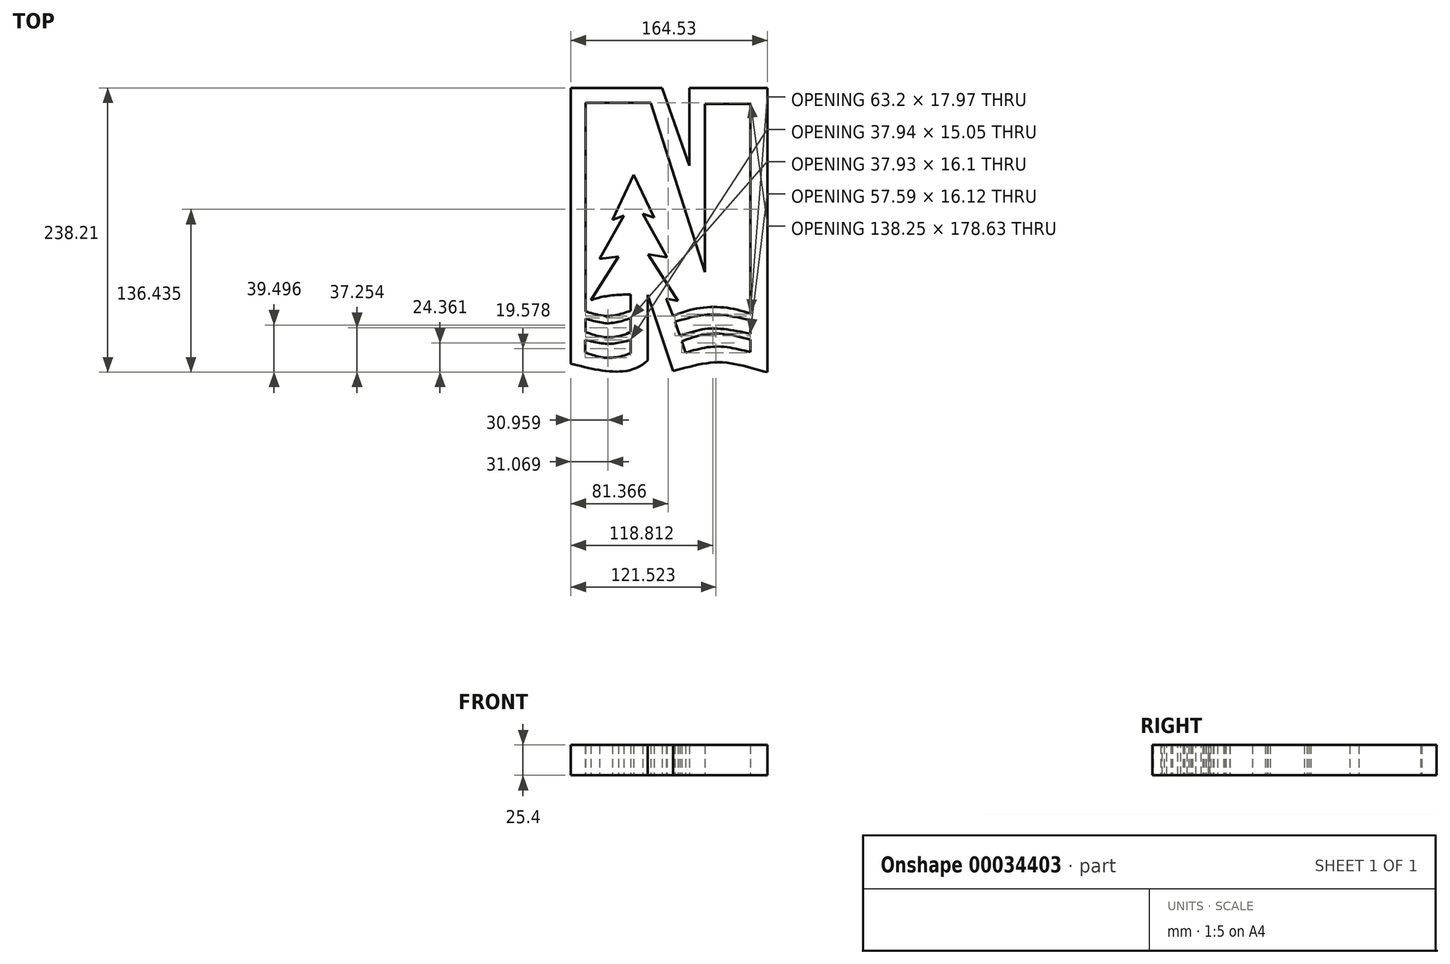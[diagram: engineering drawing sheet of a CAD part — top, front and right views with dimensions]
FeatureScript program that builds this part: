
annotation { "Feature Type Name" : "Feature", "Feature Type Description" : "" }
export const myFeature = defineFeature(function(context is Context, id is Id, definition is map)
    precondition{}
    {
        {
            var Q0;
            Q0=qCreatedBy(makeId("Top.planeOp"), FACE);
            var sketch = newSketch(context, id + "F0", { "sketchPlane" : qUnion([Q0])});
            skLineSegment(sketch, "E0", {"start": v(-73.6, 45.65) * mm, "end": v(-73.6, -185.45) * mm});
            skLineSegment(sketch, "E1", {"start": v(-73.6, 45.65) * mm, "end": v(2.84, 45.65) * mm});
            skLineSegment(sketch, "E2", {"start": v(2.84, 45.65) * mm, "end": v(25.57, -19.42) * mm});
            skLineSegment(sketch, "E3", {"start": v(25.57, -19.42) * mm, "end": v(25.57, 45.65) * mm});
            skLineSegment(sketch, "E4", {"start": v(25.57, 45.65) * mm, "end": v(90.93, 45.65) * mm});
            skLineSegment(sketch, "E5", {"start": v(90.93, 45.65) * mm, "end": v(90.93, -192.56) * mm});
            skLineSegment(sketch, "E6", {"start": v(12, -191.7) * mm, "end": v(-9.35, -127.62) * mm});
            skLineSegment(sketch, "E7", {"start": v(-9.35, -127.62) * mm, "end": v(-9.35, -182.72) * mm});
            skFitSpline(sketch, "E8", {"points": [v(90.93, -192.56) * mm, v(52.08, -184.29) * mm, v(12, -191.7) * mm], "startDerivative": vector(-76.55, 17.54) * mm, "endDerivative": vector(-80.4, -21.7) * mm});
            skFitSpline(sketch, "E9", {"points": [v(-9.35, -182.72) * mm, v(-39, -192) * mm, v(-73.6, -185.45) * mm], "startDerivative": vector(-50.09, -49.34) * mm, "endDerivative": vector(-64.77, 16.2) * mm});
            skLineSegment(sketch, "E10", {"start": v(-61.36, -141.64) * mm, "end": v(-61.36, 33.19) * mm});
            skLineSegment(sketch, "E11", {"start": v(-61.36, 33.19) * mm, "end": v(-6.84, 33.19) * mm});
            skLineSegment(sketch, "E12", {"start": v(-6.84, 33.19) * mm, "end": v(38.69, -108.6) * mm});
            skLineSegment(sketch, "E13", {"start": v(38.69, -108.6) * mm, "end": v(38.69, 32.2) * mm});
            skLineSegment(sketch, "E14", {"start": v(38.69, 32.2) * mm, "end": v(76.89, 32.2) * mm});
            skLineSegment(sketch, "E15", {"start": v(76.89, 32.2) * mm, "end": v(76.89, -143.54) * mm});
            skLineSegment(sketch, "E16", {"start": v(11.98, -145.38) * mm, "end": v(6.31, -130.91) * mm});
            skLineSegment(sketch, "E17", {"start": v(6.31, -130.91) * mm, "end": v(15.96, -132.85) * mm});
            skLineSegment(sketch, "E18", {"start": v(15.96, -132.85) * mm, "end": v(-9.1, -93.8) * mm});
            skLineSegment(sketch, "E19", {"start": v(-9.1, -93.8) * mm, "end": v(6.97, -96.35) * mm});
            skLineSegment(sketch, "E20", {"start": v(6.97, -96.35) * mm, "end": v(-13.3, -59.81) * mm});
            skLineSegment(sketch, "E21", {"start": v(-13.3, -59.81) * mm, "end": v(-4.04, -62.95) * mm});
            skLineSegment(sketch, "E22", {"start": v(-4.04, -62.95) * mm, "end": v(-20.95, -27.03) * mm});
            skLineSegment(sketch, "E23", {"start": v(-20.95, -27.03) * mm, "end": v(-38.72, -65.02) * mm});
            skLineSegment(sketch, "E24", {"start": v(-38.72, -65.02) * mm, "end": v(-29.2, -61.45) * mm});
            skLineSegment(sketch, "E25", {"start": v(-29.2, -61.45) * mm, "end": v(-49.47, -97.72) * mm});
            skLineSegment(sketch, "E26", {"start": v(-49.47, -97.72) * mm, "end": v(-33.75, -95.62) * mm});
            skLineSegment(sketch, "E27", {"start": v(-33.75, -95.62) * mm, "end": v(-56.89, -132.24) * mm});
            skFitSpline(sketch, "E28", {"points": [v(-56.89, -132.24) * mm, v(-39.31, -128.2) * mm, v(-23.46, -127.3) * mm, v(-23.54, -127.29) * mm], "startDerivative": vector(29.72, 10.9) * mm, "endDerivative": vector(-3.68, 0.29) * mm});
            skLineSegment(sketch, "E29", {"start": v(-23.46, -127.3) * mm, "end": v(-23.46, -141.03) * mm});
            skFitSpline(sketch, "E30", {"points": [v(-61.36, -141.64) * mm, v(-42.62, -145.44) * mm, v(-23.46, -141.03) * mm], "startDerivative": vector(37.66, -11.74) * mm, "endDerivative": vector(38.13, 12.9) * mm});
            skFitSpline(sketch, "E31", {"points": [v(76.89, -143.54) * mm, v(44.7, -137.98) * mm, v(11.98, -145.38) * mm], "startDerivative": vector(-64.83, 22.76) * mm, "endDerivative": vector(-61.1, -27.53) * mm});
            skLineSegment(sketch, "E32", {"start": v(-61.5, -147.62) * mm, "end": v(-61.5, -158.84) * mm});
            skLineSegment(sketch, "E33", {"start": v(-61.6, -165.46) * mm, "end": v(-61.6, -176.04) * mm});
            skLineSegment(sketch, "E34", {"start": v(-23.57, -147.25) * mm, "end": v(-23.57, -158.91) * mm});
            skLineSegment(sketch, "E35", {"start": v(-23.67, -165.58) * mm, "end": v(-23.67, -176.8) * mm});
            skLineSegment(sketch, "E36", {"start": v(17.68, -162.05) * mm, "end": v(13.61, -150.24) * mm});
            skLineSegment(sketch, "E37", {"start": v(19.13, -166.8) * mm, "end": v(22.34, -176.26) * mm});
            skLineSegment(sketch, "E38", {"start": v(76.72, -175.8) * mm, "end": v(76.72, -165.33) * mm});
            skLineSegment(sketch, "E39", {"start": v(76.81, -160.44) * mm, "end": v(76.81, -149.22) * mm});
            skFitSpline(sketch, "E40", {"points": [v(19.13, -166.8) * mm, v(45.9, -160.16) * mm, v(76.72, -165.33) * mm], "startDerivative": vector(54.42, 21.73) * mm, "endDerivative": vector(59.81, -16.82) * mm});
            skFitSpline(sketch, "E41", {"points": [v(17.68, -162.05) * mm, v(43.2, -156.01) * mm, v(76.81, -160.44) * mm], "startDerivative": vector(52.42, 17.73) * mm, "endDerivative": vector(64.82, -13.37) * mm});
            skFitSpline(sketch, "E42", {"points": [v(22.34, -176.26) * mm, v(48.3, -171.08) * mm, v(76.72, -175.8) * mm], "startDerivative": vector(52.29, 16.09) * mm, "endDerivative": vector(56.49, -14.65) * mm});
            skLineSegment(sketch, "E43", {"start": v(76.89, -143.54) * mm, "end": v(76.72, -175.8) * mm, "construction": true});
            skFitSpline(sketch, "E44", {"points": [v(76.81, -149.22) * mm, v(44.12, -144.09) * mm, v(13.61, -150.24) * mm], "startDerivative": vector(-65.02, 15.66) * mm, "endDerivative": vector(-61.92, -17.05) * mm});
            skLineSegment(sketch, "E45", {"start": v(11.98, -145.38) * mm, "end": v(22.34, -176.26) * mm, "construction": true});
            skLineSegment(sketch, "E46", {"start": v(-23.46, -141.03) * mm, "end": v(-23.67, -176.8) * mm, "construction": true});
            skLineSegment(sketch, "E47", {"start": v(-61.6, -176.04) * mm, "end": v(-61.36, -141.64) * mm, "construction": true});
            skFitSpline(sketch, "E48", {"points": [v(-61.6, -176.04) * mm, v(-43.98, -180.48) * mm, v(-23.67, -176.8) * mm], "startDerivative": vector(35.66, -12.9) * mm, "endDerivative": vector(38.58, 14.98) * mm});
            skFitSpline(sketch, "E49", {"points": [v(-23.67, -165.58) * mm, v(-41.82, -168.79) * mm, v(-61.6, -165.46) * mm], "startDerivative": vector(-36.8, -9.75) * mm, "endDerivative": vector(-39.2, 9.86) * mm});
            skFitSpline(sketch, "E50", {"points": [v(-61.5, -158.84) * mm, v(-43.36, -163.34) * mm, v(-23.57, -158.91) * mm], "startDerivative": vector(36.22, -13.26) * mm, "endDerivative": vector(35.41, 17.62) * mm});
            skFitSpline(sketch, "E51", {"points": [v(-23.57, -147.25) * mm, v(-42.07, -151.51) * mm, v(-61.5, -147.62) * mm], "startDerivative": vector(-37.28, -12.62) * mm, "endDerivative": vector(-38.49, 11.82) * mm});
            skSolve(sketch);
        }
        {
            var Q0;
            Q0 = qSketchRegion(id + "F0", true);
            extrude(context, id + "F1", {"entities" : qUnion([Q0]), "depth" : 25.4 * mm, "offsetDistance" : 25.4 * mm});
        }
    });
